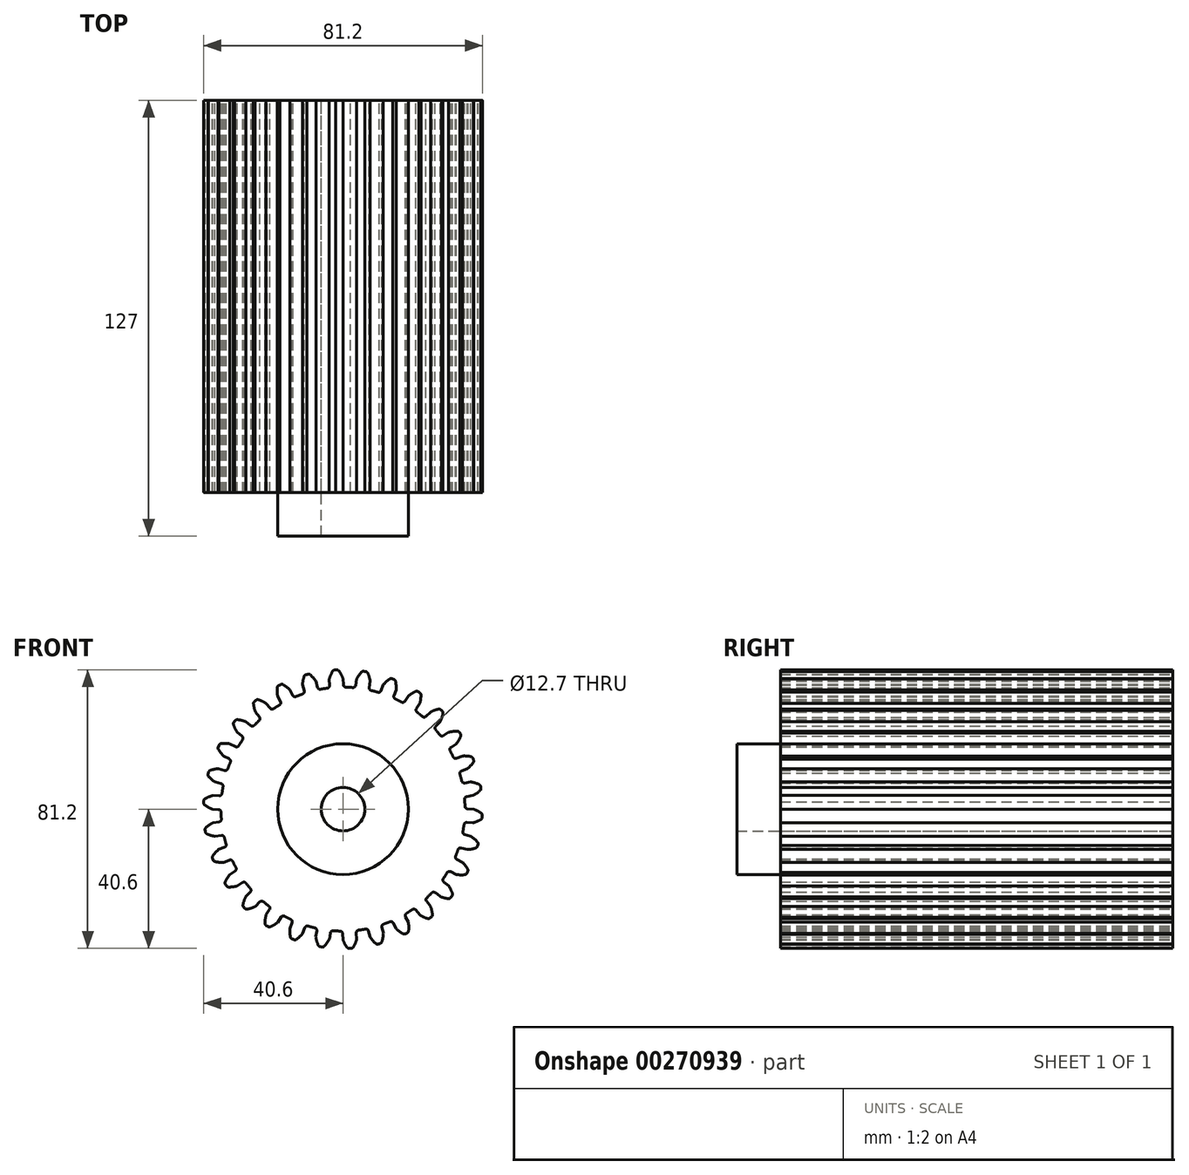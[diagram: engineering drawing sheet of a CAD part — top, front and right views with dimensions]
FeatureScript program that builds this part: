
annotation { "Feature Type Name" : "Feature", "Feature Type Description" : "" }
export const myFeature = defineFeature(function(context is Context, id is Id, definition is map)
    precondition{}
    {
        {
            var Q0;
            Q0=qCreatedBy(makeId("Front.planeOp"),FACE);
            var sketch = newSketch(context, id + "F0", { "sketchPlane" : qUnion([Q0])});
            skCircle(sketch, "E0", {"center": v(0, 0) * mm, "radius": 6.35 * mm});
            skArc(sketch, "E1", {"start": v(-11.8, 33.55) * mm, "mid": v(-12.74, 33.2) * mm, "end": v(-13.69, 32.82) * mm});
            skArc(sketch, "E2.trimOffspring", {"start": v(0, 38.1) * mm, "mid": v(-0.51, 39.23) * mm, "end": v(-1.18, 40.29) * mm});
            skLineSegment(sketch, "E3", {"start": v(-1.82, 40.6) * mm, "end": v(-2.13, 40.6) * mm});
            skLineSegment(sketch, "E4", {"start": v(0, 38.1) * mm, "end": v(0.1, 36.27) * mm});
            skLineSegment(sketch, "E5.MirrorCS", {"start": v(-2.43, 40.57) * mm, "end": v(-2.13, 40.6) * mm});
            skArc(sketch, "E6.MirrorCS", {"start": v(-4, 37.9) * mm, "mid": v(-3.59, 39.07) * mm, "end": v(-3.04, 40.2) * mm});
            skLineSegment(sketch, "E7.MirrorCS", {"start": v(-4, 37.9) * mm, "end": v(-3.9, 36.06) * mm});
            skArc(sketch, "E8.1.0", {"start": v(-11.78, 36.23) * mm, "mid": v(-11.63, 37.47) * mm, "end": v(-11.33, 38.68) * mm});
            skLineSegment(sketch, "E8.1.1", {"start": v(-11.78, 36.23) * mm, "end": v(-11.3, 34.46) * mm});
            skLineSegment(sketch, "E8.1.2", {"start": v(-7.91, 37.27) * mm, "end": v(-7.44, 35.5) * mm});
            skArc(sketch, "E8.1.3", {"start": v(-7.91, 37.27) * mm, "mid": v(-8.66, 38.27) * mm, "end": v(-9.53, 39.16) * mm});
            skLineSegment(sketch, "E8.1.4", {"start": v(-10.23, 39.33) * mm, "end": v(-10.52, 39.26) * mm});
            skLineSegment(sketch, "E8.1.5", {"start": v(-10.81, 39.18) * mm, "end": v(-10.52, 39.26) * mm});
            skArc(sketch, "E8.2.0", {"start": v(-19.06, 33) * mm, "mid": v(-19.17, 34.23) * mm, "end": v(-19.12, 35.48) * mm});
            skLineSegment(sketch, "E8.2.1", {"start": v(-19.06, 33) * mm, "end": v(-18.23, 31.36) * mm});
            skLineSegment(sketch, "E8.2.2", {"start": v(-15.49, 34.8) * mm, "end": v(-14.66, 33.18) * mm});
            skArc(sketch, "E8.2.3", {"start": v(-15.49, 34.8) * mm, "mid": v(-16.43, 35.63) * mm, "end": v(-17.47, 36.32) * mm});
            skLineSegment(sketch, "E8.2.4", {"start": v(-18.18, 36.35) * mm, "end": v(-18.45, 36.22) * mm});
            skLineSegment(sketch, "E8.2.5", {"start": v(-18.72, 36.07) * mm, "end": v(-18.45, 36.22) * mm});
            skArc(sketch, "E9.2.3.0", {"start": v(-25.5, 28.3) * mm, "mid": v(-25.87, 29.5) * mm, "end": v(-26.08, 30.73) * mm});
            skLineSegment(sketch, "E9.4.3.0", {"start": v(-25.5, 28.3) * mm, "end": v(-24.35, 26.89) * mm});
            skLineSegment(sketch, "E9.7.3.0", {"start": v(-22.39, 30.83) * mm, "end": v(-21.24, 29.4) * mm});
            skArc(sketch, "E9.10.3.0", {"start": v(-22.39, 30.83) * mm, "mid": v(-23.48, 31.44) * mm, "end": v(-24.64, 31.9) * mm});
            skLineSegment(sketch, "E9.14.3.0", {"start": v(-25.34, 31.77) * mm, "end": v(-25.58, 31.59) * mm});
            skLineSegment(sketch, "E9.17.3.0", {"start": v(-25.81, 31.4) * mm, "end": v(-25.58, 31.59) * mm});
            skArc(sketch, "E9.2.4.0", {"start": v(-30.83, 22.39) * mm, "mid": v(-31.44, 23.48) * mm, "end": v(-31.9, 24.64) * mm});
            skLineSegment(sketch, "E9.4.4.0", {"start": v(-30.83, 22.39) * mm, "end": v(-29.4, 21.24) * mm});
            skLineSegment(sketch, "E9.7.4.0", {"start": v(-28.3, 25.5) * mm, "end": v(-26.89, 24.35) * mm});
            skArc(sketch, "E9.10.4.0", {"start": v(-28.3, 25.5) * mm, "mid": v(-29.5, 25.87) * mm, "end": v(-30.73, 26.08) * mm});
            skLineSegment(sketch, "E9.14.4.0", {"start": v(-31.4, 25.81) * mm, "end": v(-31.59, 25.58) * mm});
            skLineSegment(sketch, "E9.17.4.0", {"start": v(-31.77, 25.34) * mm, "end": v(-31.59, 25.58) * mm});
            skArc(sketch, "E9.2.5.0", {"start": v(-34.8, 15.49) * mm, "mid": v(-35.63, 16.43) * mm, "end": v(-36.32, 17.47) * mm});
            skLineSegment(sketch, "E9.4.5.0", {"start": v(-34.8, 15.49) * mm, "end": v(-33.18, 14.66) * mm});
            skLineSegment(sketch, "E9.7.5.0", {"start": v(-33, 19.06) * mm, "end": v(-31.36, 18.23) * mm});
            skArc(sketch, "E9.10.5.0", {"start": v(-33, 19.06) * mm, "mid": v(-34.23, 19.17) * mm, "end": v(-35.48, 19.12) * mm});
            skLineSegment(sketch, "E9.14.5.0", {"start": v(-36.07, 18.72) * mm, "end": v(-36.22, 18.45) * mm});
            skLineSegment(sketch, "E9.17.5.0", {"start": v(-36.35, 18.18) * mm, "end": v(-36.22, 18.45) * mm});
            skArc(sketch, "E9.2.6.0", {"start": v(-37.27, 7.91) * mm, "mid": v(-38.27, 8.66) * mm, "end": v(-39.16, 9.53) * mm});
            skLineSegment(sketch, "E9.4.6.0", {"start": v(-37.27, 7.91) * mm, "end": v(-35.5, 7.44) * mm});
            skLineSegment(sketch, "E9.7.6.0", {"start": v(-36.23, 11.78) * mm, "end": v(-34.46, 11.3) * mm});
            skArc(sketch, "E9.10.6.0", {"start": v(-36.23, 11.78) * mm, "mid": v(-37.47, 11.63) * mm, "end": v(-38.68, 11.33) * mm});
            skLineSegment(sketch, "E9.14.6.0", {"start": v(-39.18, 10.81) * mm, "end": v(-39.26, 10.52) * mm});
            skLineSegment(sketch, "E9.17.6.0", {"start": v(-39.33, 10.23) * mm, "end": v(-39.26, 10.52) * mm});
            skArc(sketch, "E9.2.7.0", {"start": v(-38.1, 0) * mm, "mid": v(-39.23, 0.51) * mm, "end": v(-40.29, 1.18) * mm});
            skLineSegment(sketch, "E9.4.7.0", {"start": v(-38.1, 0) * mm, "end": v(-36.27, -0.1) * mm});
            skLineSegment(sketch, "E9.7.7.0", {"start": v(-37.9, 4) * mm, "end": v(-36.06, 3.9) * mm});
            skArc(sketch, "E9.10.7.0", {"start": v(-37.9, 4) * mm, "mid": v(-39.07, 3.59) * mm, "end": v(-40.2, 3.04) * mm});
            skLineSegment(sketch, "E9.14.7.0", {"start": v(-40.57, 2.43) * mm, "end": v(-40.6, 2.13) * mm});
            skLineSegment(sketch, "E9.17.7.0", {"start": v(-40.6, 1.82) * mm, "end": v(-40.6, 2.13) * mm});
            skArc(sketch, "E9.2.8.0", {"start": v(-37.27, -7.93) * mm, "mid": v(-38.48, -7.65) * mm, "end": v(-39.65, -7.22) * mm});
            skLineSegment(sketch, "E9.4.8.0", {"start": v(-37.27, -7.93) * mm, "end": v(-35.46, -7.64) * mm});
            skLineSegment(sketch, "E9.7.8.0", {"start": v(-37.9, -3.97) * mm, "end": v(-36.08, -3.69) * mm});
            skArc(sketch, "E9.10.8.0", {"start": v(-37.9, -3.97) * mm, "mid": v(-38.96, -4.61) * mm, "end": v(-39.94, -5.39) * mm});
            skLineSegment(sketch, "E9.14.8.0", {"start": v(-40.19, -6.06) * mm, "end": v(-40.15, -6.36) * mm});
            skLineSegment(sketch, "E9.17.8.0", {"start": v(-40.1, -6.66) * mm, "end": v(-40.15, -6.36) * mm});
            skArc(sketch, "E9.2.9.0", {"start": v(-34.8, -15.5) * mm, "mid": v(-36.05, -15.49) * mm, "end": v(-37.29, -15.3) * mm});
            skLineSegment(sketch, "E9.4.9.0", {"start": v(-34.8, -15.5) * mm, "end": v(-33.1, -14.85) * mm});
            skLineSegment(sketch, "E9.7.9.0", {"start": v(-36.24, -11.77) * mm, "end": v(-34.53, -11.1) * mm});
            skArc(sketch, "E9.10.9.0", {"start": v(-36.24, -11.77) * mm, "mid": v(-37.15, -12.61) * mm, "end": v(-37.95, -13.57) * mm});
            skLineSegment(sketch, "E9.14.9.0", {"start": v(-38.05, -14.28) * mm, "end": v(-37.95, -14.57) * mm});
            skLineSegment(sketch, "E9.17.9.0", {"start": v(-37.83, -14.85) * mm, "end": v(-37.95, -14.57) * mm});
            skArc(sketch, "E9.2.10.0", {"start": v(-30.82, -22.4) * mm, "mid": v(-32.04, -22.64) * mm, "end": v(-33.29, -22.73) * mm});
            skLineSegment(sketch, "E9.4.10.0", {"start": v(-30.82, -22.4) * mm, "end": v(-29.28, -21.4) * mm});
            skLineSegment(sketch, "E9.7.10.0", {"start": v(-33, -19.04) * mm, "end": v(-31.46, -18.05) * mm});
            skArc(sketch, "E9.10.10.0", {"start": v(-33, -19.04) * mm, "mid": v(-33.72, -20.06) * mm, "end": v(-34.3, -21.17) * mm});
            skLineSegment(sketch, "E9.14.10.0", {"start": v(-34.25, -21.88) * mm, "end": v(-34.09, -22.14) * mm});
            skLineSegment(sketch, "E9.17.10.0", {"start": v(-33.92, -22.39) * mm, "end": v(-34.09, -22.14) * mm});
            skArc(sketch, "E9.2.11.0", {"start": v(-25.49, -28.32) * mm, "mid": v(-26.63, -28.81) * mm, "end": v(-27.84, -29.15) * mm});
            skLineSegment(sketch, "E9.4.11.0", {"start": v(-25.49, -28.32) * mm, "end": v(-24.2, -27.03) * mm});
            skLineSegment(sketch, "E9.7.11.0", {"start": v(-28.32, -25.49) * mm, "end": v(-27.03, -24.2) * mm});
            skArc(sketch, "E9.10.11.0", {"start": v(-28.32, -25.49) * mm, "mid": v(-28.81, -26.63) * mm, "end": v(-29.15, -27.84) * mm});
            skLineSegment(sketch, "E9.14.11.0", {"start": v(-28.95, -28.52) * mm, "end": v(-28.74, -28.74) * mm});
            skLineSegment(sketch, "E9.17.11.0", {"start": v(-28.52, -28.95) * mm, "end": v(-28.74, -28.74) * mm});
            skArc(sketch, "E9.2.12.0", {"start": v(-19.04, -33) * mm, "mid": v(-20.06, -33.72) * mm, "end": v(-21.17, -34.3) * mm});
            skLineSegment(sketch, "E9.4.12.0", {"start": v(-19.04, -33) * mm, "end": v(-18.05, -31.46) * mm});
            skLineSegment(sketch, "E9.7.12.0", {"start": v(-22.4, -30.82) * mm, "end": v(-21.4, -29.28) * mm});
            skArc(sketch, "E9.10.12.0", {"start": v(-22.4, -30.82) * mm, "mid": v(-22.64, -32.04) * mm, "end": v(-22.73, -33.29) * mm});
            skLineSegment(sketch, "E9.14.12.0", {"start": v(-22.39, -33.92) * mm, "end": v(-22.14, -34.09) * mm});
            skLineSegment(sketch, "E9.17.12.0", {"start": v(-21.88, -34.25) * mm, "end": v(-22.14, -34.09) * mm});
            skArc(sketch, "E9.2.13.0", {"start": v(-11.77, -36.24) * mm, "mid": v(-12.61, -37.15) * mm, "end": v(-13.57, -37.95) * mm});
            skLineSegment(sketch, "E9.4.13.0", {"start": v(-11.77, -36.24) * mm, "end": v(-11.1, -34.53) * mm});
            skLineSegment(sketch, "E9.7.13.0", {"start": v(-15.5, -34.8) * mm, "end": v(-14.85, -33.1) * mm});
            skArc(sketch, "E9.10.13.0", {"start": v(-15.5, -34.8) * mm, "mid": v(-15.49, -36.05) * mm, "end": v(-15.3, -37.29) * mm});
            skLineSegment(sketch, "E9.14.13.0", {"start": v(-14.85, -37.83) * mm, "end": v(-14.57, -37.95) * mm});
            skLineSegment(sketch, "E9.17.13.0", {"start": v(-14.28, -38.05) * mm, "end": v(-14.57, -37.95) * mm});
            skArc(sketch, "E9.2.14.0", {"start": v(-3.97, -37.9) * mm, "mid": v(-4.61, -38.96) * mm, "end": v(-5.39, -39.94) * mm});
            skLineSegment(sketch, "E9.4.14.0", {"start": v(-3.97, -37.9) * mm, "end": v(-3.69, -36.08) * mm});
            skLineSegment(sketch, "E9.7.14.0", {"start": v(-7.93, -37.27) * mm, "end": v(-7.64, -35.46) * mm});
            skArc(sketch, "E9.10.14.0", {"start": v(-7.93, -37.27) * mm, "mid": v(-7.65, -38.48) * mm, "end": v(-7.22, -39.65) * mm});
            skLineSegment(sketch, "E9.14.14.0", {"start": v(-6.66, -40.1) * mm, "end": v(-6.36, -40.15) * mm});
            skLineSegment(sketch, "E9.17.14.0", {"start": v(-6.06, -40.19) * mm, "end": v(-6.36, -40.15) * mm});
            skArc(sketch, "E9.2.15.0", {"start": v(4, -37.9) * mm, "mid": v(3.59, -39.07) * mm, "end": v(3.04, -40.2) * mm});
            skLineSegment(sketch, "E9.4.15.0", {"start": v(4, -37.9) * mm, "end": v(3.9, -36.06) * mm});
            skLineSegment(sketch, "E9.7.15.0", {"start": v(0, -38.1) * mm, "end": v(-0.1, -36.27) * mm});
            skArc(sketch, "E9.10.15.0", {"start": v(0, -38.1) * mm, "mid": v(0.51, -39.23) * mm, "end": v(1.18, -40.29) * mm});
            skLineSegment(sketch, "E9.14.15.0", {"start": v(1.82, -40.6) * mm, "end": v(2.13, -40.6) * mm});
            skLineSegment(sketch, "E9.17.15.0", {"start": v(2.43, -40.57) * mm, "end": v(2.13, -40.6) * mm});
            skArc(sketch, "E9.2.16.0", {"start": v(11.78, -36.23) * mm, "mid": v(11.63, -37.47) * mm, "end": v(11.33, -38.68) * mm});
            skLineSegment(sketch, "E9.4.16.0", {"start": v(11.78, -36.23) * mm, "end": v(11.3, -34.46) * mm});
            skLineSegment(sketch, "E9.7.16.0", {"start": v(7.91, -37.27) * mm, "end": v(7.44, -35.5) * mm});
            skArc(sketch, "E9.10.16.0", {"start": v(7.91, -37.27) * mm, "mid": v(8.66, -38.27) * mm, "end": v(9.53, -39.16) * mm});
            skLineSegment(sketch, "E9.14.16.0", {"start": v(10.23, -39.33) * mm, "end": v(10.52, -39.26) * mm});
            skLineSegment(sketch, "E9.17.16.0", {"start": v(10.81, -39.18) * mm, "end": v(10.52, -39.26) * mm});
            skArc(sketch, "E9.2.17.0", {"start": v(19.06, -33) * mm, "mid": v(19.17, -34.23) * mm, "end": v(19.12, -35.48) * mm});
            skLineSegment(sketch, "E9.4.17.0", {"start": v(19.06, -33) * mm, "end": v(18.23, -31.36) * mm});
            skLineSegment(sketch, "E9.7.17.0", {"start": v(15.49, -34.8) * mm, "end": v(14.66, -33.18) * mm});
            skArc(sketch, "E9.10.17.0", {"start": v(15.49, -34.8) * mm, "mid": v(16.43, -35.63) * mm, "end": v(17.47, -36.32) * mm});
            skLineSegment(sketch, "E9.14.17.0", {"start": v(18.18, -36.35) * mm, "end": v(18.45, -36.22) * mm});
            skLineSegment(sketch, "E9.17.17.0", {"start": v(18.72, -36.07) * mm, "end": v(18.45, -36.22) * mm});
            skArc(sketch, "E9.2.18.0", {"start": v(25.5, -28.3) * mm, "mid": v(25.87, -29.5) * mm, "end": v(26.08, -30.73) * mm});
            skLineSegment(sketch, "E9.4.18.0", {"start": v(25.5, -28.3) * mm, "end": v(24.35, -26.89) * mm});
            skLineSegment(sketch, "E9.7.18.0", {"start": v(22.39, -30.83) * mm, "end": v(21.24, -29.4) * mm});
            skArc(sketch, "E9.10.18.0", {"start": v(22.39, -30.83) * mm, "mid": v(23.48, -31.44) * mm, "end": v(24.64, -31.9) * mm});
            skLineSegment(sketch, "E9.14.18.0", {"start": v(25.34, -31.77) * mm, "end": v(25.58, -31.59) * mm});
            skLineSegment(sketch, "E9.17.18.0", {"start": v(25.81, -31.4) * mm, "end": v(25.58, -31.59) * mm});
            skArc(sketch, "E9.2.19.0", {"start": v(30.83, -22.39) * mm, "mid": v(31.44, -23.48) * mm, "end": v(31.9, -24.64) * mm});
            skLineSegment(sketch, "E9.4.19.0", {"start": v(30.83, -22.39) * mm, "end": v(29.4, -21.24) * mm});
            skLineSegment(sketch, "E9.7.19.0", {"start": v(28.3, -25.5) * mm, "end": v(26.89, -24.35) * mm});
            skArc(sketch, "E9.10.19.0", {"start": v(28.3, -25.5) * mm, "mid": v(29.5, -25.87) * mm, "end": v(30.73, -26.08) * mm});
            skLineSegment(sketch, "E9.14.19.0", {"start": v(31.4, -25.81) * mm, "end": v(31.59, -25.58) * mm});
            skLineSegment(sketch, "E9.17.19.0", {"start": v(31.77, -25.34) * mm, "end": v(31.59, -25.58) * mm});
            skArc(sketch, "E9.2.20.0", {"start": v(34.8, -15.49) * mm, "mid": v(35.63, -16.43) * mm, "end": v(36.32, -17.47) * mm});
            skLineSegment(sketch, "E9.4.20.0", {"start": v(34.8, -15.49) * mm, "end": v(33.18, -14.66) * mm});
            skLineSegment(sketch, "E9.7.20.0", {"start": v(33, -19.06) * mm, "end": v(31.36, -18.23) * mm});
            skArc(sketch, "E9.10.20.0", {"start": v(33, -19.06) * mm, "mid": v(34.23, -19.17) * mm, "end": v(35.48, -19.12) * mm});
            skLineSegment(sketch, "E9.14.20.0", {"start": v(36.07, -18.72) * mm, "end": v(36.22, -18.45) * mm});
            skLineSegment(sketch, "E9.17.20.0", {"start": v(36.35, -18.18) * mm, "end": v(36.22, -18.45) * mm});
            skArc(sketch, "E9.2.21.0", {"start": v(37.27, -7.91) * mm, "mid": v(38.27, -8.66) * mm, "end": v(39.16, -9.53) * mm});
            skLineSegment(sketch, "E9.4.21.0", {"start": v(37.27, -7.91) * mm, "end": v(35.5, -7.44) * mm});
            skLineSegment(sketch, "E9.7.21.0", {"start": v(36.23, -11.78) * mm, "end": v(34.46, -11.3) * mm});
            skArc(sketch, "E9.10.21.0", {"start": v(36.23, -11.78) * mm, "mid": v(37.47, -11.63) * mm, "end": v(38.68, -11.33) * mm});
            skLineSegment(sketch, "E9.14.21.0", {"start": v(39.18, -10.81) * mm, "end": v(39.26, -10.52) * mm});
            skLineSegment(sketch, "E9.17.21.0", {"start": v(39.33, -10.23) * mm, "end": v(39.26, -10.52) * mm});
            skArc(sketch, "E9.2.22.0", {"start": v(38.1, 0) * mm, "mid": v(39.23, -0.51) * mm, "end": v(40.29, -1.18) * mm});
            skLineSegment(sketch, "E9.4.22.0", {"start": v(38.1, 0) * mm, "end": v(36.27, 0.1) * mm});
            skLineSegment(sketch, "E9.7.22.0", {"start": v(37.9, -4) * mm, "end": v(36.06, -3.9) * mm});
            skArc(sketch, "E9.10.22.0", {"start": v(37.9, -4) * mm, "mid": v(39.07, -3.59) * mm, "end": v(40.2, -3.04) * mm});
            skLineSegment(sketch, "E9.14.22.0", {"start": v(40.57, -2.43) * mm, "end": v(40.59, -2.14) * mm});
            skLineSegment(sketch, "E9.17.22.0", {"start": v(40.6, -1.82) * mm, "end": v(40.6, -2.11) * mm});
            skArc(sketch, "E9.2.23.0", {"start": v(37.27, 7.93) * mm, "mid": v(38.48, 7.65) * mm, "end": v(39.65, 7.22) * mm});
            skLineSegment(sketch, "E9.4.23.0", {"start": v(37.27, 7.93) * mm, "end": v(35.46, 7.64) * mm});
            skLineSegment(sketch, "E9.7.23.0", {"start": v(37.9, 3.97) * mm, "end": v(36.08, 3.69) * mm});
            skArc(sketch, "E9.10.23.0", {"start": v(37.9, 3.97) * mm, "mid": v(38.96, 4.61) * mm, "end": v(39.94, 5.39) * mm});
            skLineSegment(sketch, "E9.14.23.0", {"start": v(40.19, 6.06) * mm, "end": v(40.15, 6.36) * mm});
            skLineSegment(sketch, "E9.17.23.0", {"start": v(40.1, 6.66) * mm, "end": v(40.15, 6.36) * mm});
            skArc(sketch, "E9.2.24.0", {"start": v(34.8, 15.5) * mm, "mid": v(36.05, 15.49) * mm, "end": v(37.29, 15.3) * mm});
            skLineSegment(sketch, "E9.4.24.0", {"start": v(34.8, 15.5) * mm, "end": v(33.1, 14.85) * mm});
            skLineSegment(sketch, "E9.7.24.0", {"start": v(36.24, 11.77) * mm, "end": v(34.53, 11.1) * mm});
            skArc(sketch, "E9.10.24.0", {"start": v(36.24, 11.77) * mm, "mid": v(37.15, 12.61) * mm, "end": v(37.95, 13.57) * mm});
            skLineSegment(sketch, "E9.14.24.0", {"start": v(38.05, 14.28) * mm, "end": v(37.95, 14.57) * mm});
            skLineSegment(sketch, "E9.17.24.0", {"start": v(37.83, 14.85) * mm, "end": v(37.95, 14.57) * mm});
            skArc(sketch, "E9.2.25.0", {"start": v(30.82, 22.4) * mm, "mid": v(32.04, 22.64) * mm, "end": v(33.29, 22.73) * mm});
            skLineSegment(sketch, "E9.4.25.0", {"start": v(30.82, 22.4) * mm, "end": v(29.28, 21.4) * mm});
            skLineSegment(sketch, "E9.7.25.0", {"start": v(33, 19.04) * mm, "end": v(31.46, 18.05) * mm});
            skArc(sketch, "E9.10.25.0", {"start": v(33, 19.04) * mm, "mid": v(33.72, 20.06) * mm, "end": v(34.3, 21.17) * mm});
            skLineSegment(sketch, "E9.14.25.0", {"start": v(34.25, 21.88) * mm, "end": v(34.09, 22.14) * mm});
            skLineSegment(sketch, "E9.17.25.0", {"start": v(33.92, 22.39) * mm, "end": v(34.09, 22.14) * mm});
            skArc(sketch, "E9.2.26.0", {"start": v(25.49, 28.32) * mm, "mid": v(26.63, 28.81) * mm, "end": v(27.84, 29.15) * mm});
            skLineSegment(sketch, "E9.4.26.0", {"start": v(25.49, 28.32) * mm, "end": v(24.2, 27.03) * mm});
            skLineSegment(sketch, "E9.7.26.0", {"start": v(28.32, 25.49) * mm, "end": v(27.03, 24.2) * mm});
            skArc(sketch, "E9.10.26.0", {"start": v(28.32, 25.49) * mm, "mid": v(28.81, 26.63) * mm, "end": v(29.15, 27.84) * mm});
            skLineSegment(sketch, "E9.14.26.0", {"start": v(28.95, 28.52) * mm, "end": v(28.74, 28.74) * mm});
            skLineSegment(sketch, "E9.17.26.0", {"start": v(28.52, 28.95) * mm, "end": v(28.74, 28.74) * mm});
            skArc(sketch, "E9.2.27.0", {"start": v(19.04, 33) * mm, "mid": v(20.06, 33.72) * mm, "end": v(21.17, 34.3) * mm});
            skLineSegment(sketch, "E9.4.27.0", {"start": v(19.04, 33) * mm, "end": v(18.05, 31.46) * mm});
            skLineSegment(sketch, "E9.7.27.0", {"start": v(22.4, 30.82) * mm, "end": v(21.4, 29.28) * mm});
            skArc(sketch, "E9.10.27.0", {"start": v(22.4, 30.82) * mm, "mid": v(22.64, 32.04) * mm, "end": v(22.73, 33.29) * mm});
            skLineSegment(sketch, "E9.14.27.0", {"start": v(22.39, 33.92) * mm, "end": v(22.14, 34.09) * mm});
            skLineSegment(sketch, "E9.17.27.0", {"start": v(21.88, 34.25) * mm, "end": v(22.14, 34.09) * mm});
            skArc(sketch, "E9.2.28.0", {"start": v(11.77, 36.24) * mm, "mid": v(12.61, 37.15) * mm, "end": v(13.57, 37.95) * mm});
            skLineSegment(sketch, "E9.4.28.0", {"start": v(11.77, 36.24) * mm, "end": v(11.1, 34.53) * mm});
            skLineSegment(sketch, "E9.7.28.0", {"start": v(15.5, 34.8) * mm, "end": v(14.85, 33.1) * mm});
            skArc(sketch, "E9.10.28.0", {"start": v(15.5, 34.8) * mm, "mid": v(15.49, 36.05) * mm, "end": v(15.3, 37.29) * mm});
            skLineSegment(sketch, "E9.14.28.0", {"start": v(14.85, 37.83) * mm, "end": v(14.57, 37.95) * mm});
            skLineSegment(sketch, "E9.17.28.0", {"start": v(14.28, 38.05) * mm, "end": v(14.57, 37.95) * mm});
            skArc(sketch, "E9.2.29.0", {"start": v(3.97, 37.9) * mm, "mid": v(4.61, 38.96) * mm, "end": v(5.39, 39.94) * mm});
            skLineSegment(sketch, "E9.4.29.0", {"start": v(3.97, 37.9) * mm, "end": v(3.69, 36.08) * mm});
            skLineSegment(sketch, "E9.7.29.0", {"start": v(7.93, 37.27) * mm, "end": v(7.64, 35.46) * mm});
            skArc(sketch, "E9.10.29.0", {"start": v(7.93, 37.27) * mm, "mid": v(7.65, 38.48) * mm, "end": v(7.22, 39.65) * mm});
            skLineSegment(sketch, "E9.14.29.0", {"start": v(6.66, 40.1) * mm, "end": v(6.36, 40.15) * mm});
            skLineSegment(sketch, "E9.17.29.0", {"start": v(6.06, 40.19) * mm, "end": v(6.36, 40.15) * mm});
            skArc(sketch, "E10.trimOffspring", {"start": v(-4.56, 35.27) * mm, "mid": v(-5.56, 35.12) * mm, "end": v(-6.56, 34.95) * mm});
            skArc(sketch, "E11.trimOffspring", {"start": v(2.87, 35.44) * mm, "mid": v(1.86, 35.51) * mm, "end": v(0.85, 35.55) * mm});
            skArc(sketch, "E12.trimOffspring", {"start": v(10.18, 34.07) * mm, "mid": v(9.2, 34.35) * mm, "end": v(8.22, 34.6) * mm});
            skArc(sketch, "E13.trimOffspring", {"start": v(17.04, 31.21) * mm, "mid": v(16.14, 31.68) * mm, "end": v(15.23, 32.13) * mm});
            skArc(sketch, "E14.trimOffspring", {"start": v(23.16, 26.99) * mm, "mid": v(22.38, 27.64) * mm, "end": v(21.58, 28.26) * mm});
            skArc(sketch, "E15.trimOffspring", {"start": v(28.26, 21.58) * mm, "mid": v(27.64, 22.38) * mm, "end": v(26.99, 23.16) * mm});
            skArc(sketch, "E16.trimOffspring", {"start": v(32.13, 15.23) * mm, "mid": v(31.68, 16.14) * mm, "end": v(31.21, 17.04) * mm});
            skArc(sketch, "E17.trimOffspring", {"start": v(34.6, 8.22) * mm, "mid": v(34.35, 9.2) * mm, "end": v(34.07, 10.18) * mm});
            skArc(sketch, "E18.trimOffspring", {"start": v(35.55, 0.85) * mm, "mid": v(35.51, 1.86) * mm, "end": v(35.44, 2.87) * mm});
            skArc(sketch, "E19.trimOffspring", {"start": v(34.95, -6.56) * mm, "mid": v(35.12, -5.56) * mm, "end": v(35.27, -4.56) * mm});
            skArc(sketch, "E20.trimOffspring", {"start": v(32.82, -13.69) * mm, "mid": v(33.2, -12.74) * mm, "end": v(33.55, -11.8) * mm});
            skArc(sketch, "E21.trimOffspring", {"start": v(29.26, -20.21) * mm, "mid": v(29.82, -19.37) * mm, "end": v(30.36, -18.5) * mm});
            skArc(sketch, "E22.trimOffspring", {"start": v(24.42, -25.85) * mm, "mid": v(25.14, -25.14) * mm, "end": v(25.85, -24.42) * mm});
            skArc(sketch, "E23.trimOffspring", {"start": v(18.5, -30.36) * mm, "mid": v(19.37, -29.82) * mm, "end": v(20.21, -29.26) * mm});
            skArc(sketch, "E24.trimOffspring", {"start": v(11.8, -33.55) * mm, "mid": v(12.74, -33.2) * mm, "end": v(13.69, -32.82) * mm});
            skArc(sketch, "E25.trimOffspring", {"start": v(4.56, -35.27) * mm, "mid": v(5.56, -35.12) * mm, "end": v(6.56, -34.95) * mm});
            skArc(sketch, "E26.trimOffspring", {"start": v(-2.87, -35.44) * mm, "mid": v(-1.86, -35.51) * mm, "end": v(-0.85, -35.55) * mm});
            skArc(sketch, "E27.trimOffspring", {"start": v(-10.18, -34.07) * mm, "mid": v(-9.2, -34.35) * mm, "end": v(-8.22, -34.6) * mm});
            skArc(sketch, "E28.trimOffspring", {"start": v(-17.04, -31.21) * mm, "mid": v(-16.14, -31.68) * mm, "end": v(-15.23, -32.13) * mm});
            skArc(sketch, "E29.trimOffspring", {"start": v(-23.16, -26.99) * mm, "mid": v(-22.38, -27.64) * mm, "end": v(-21.58, -28.26) * mm});
            skArc(sketch, "E30.trimOffspring", {"start": v(-28.26, -21.58) * mm, "mid": v(-27.64, -22.38) * mm, "end": v(-26.99, -23.16) * mm});
            skArc(sketch, "E31.trimOffspring", {"start": v(-32.13, -15.23) * mm, "mid": v(-31.68, -16.14) * mm, "end": v(-31.21, -17.04) * mm});
            skArc(sketch, "E32.trimOffspring", {"start": v(-34.6, -8.22) * mm, "mid": v(-34.35, -9.2) * mm, "end": v(-34.07, -10.18) * mm});
            skArc(sketch, "E33.trimOffspring", {"start": v(-35.55, -0.85) * mm, "mid": v(-35.51, -1.86) * mm, "end": v(-35.44, -2.87) * mm});
            skArc(sketch, "E34.trimOffspring", {"start": v(-34.95, 6.56) * mm, "mid": v(-35.12, 5.56) * mm, "end": v(-35.27, 4.56) * mm});
            skArc(sketch, "E35.trimOffspring", {"start": v(-32.82, 13.69) * mm, "mid": v(-33.2, 12.74) * mm, "end": v(-33.55, 11.8) * mm});
            skArc(sketch, "E36.trimOffspring", {"start": v(-29.26, 20.21) * mm, "mid": v(-29.82, 19.37) * mm, "end": v(-30.36, 18.5) * mm});
            skArc(sketch, "E37.trimOffspring", {"start": v(-24.42, 25.85) * mm, "mid": v(-25.14, 25.14) * mm, "end": v(-25.85, 24.42) * mm});
            skArc(sketch, "E38.trimOffspring", {"start": v(-18.5, 30.36) * mm, "mid": v(-19.37, 29.82) * mm, "end": v(-20.21, 29.26) * mm});
            skPoint(sketch, "E39.visualSharp", {"position": v(-26.11, 31.14) * mm});
            skArc(sketch, "E39.filletArc", {"start": v(-25.81, 31.4) * mm, "mid": v(-26.03, 31.1) * mm, "end": v(-26.08, 30.73) * mm});
            skPoint(sketch, "E40.visualSharp", {"position": v(-25.03, 32.02) * mm});
            skArc(sketch, "E40.filletArc", {"start": v(-24.64, 31.9) * mm, "mid": v(-25, 31.92) * mm, "end": v(-25.34, 31.77) * mm});
            skPoint(sketch, "E41.visualSharp", {"position": v(-23.9, 26.33) * mm});
            skArc(sketch, "E41.filletArc", {"start": v(-24.42, 25.85) * mm, "mid": v(-24.18, 26.36) * mm, "end": v(-24.35, 26.89) * mm});
            skPoint(sketch, "E42.visualSharp", {"position": v(-20.79, 28.85) * mm});
            skArc(sketch, "E42.filletArc", {"start": v(-21.24, 29.4) * mm, "mid": v(-20.75, 29.13) * mm, "end": v(-20.21, 29.26) * mm});
            skPoint(sketch, "E43.visualSharp", {"position": v(-19.07, 35.89) * mm});
            skArc(sketch, "E43.filletArc", {"start": v(-18.72, 36.07) * mm, "mid": v(-19, 35.83) * mm, "end": v(-19.12, 35.48) * mm});
            skPoint(sketch, "E44.visualSharp", {"position": v(-17.83, 36.52) * mm});
            skArc(sketch, "E44.filletArc", {"start": v(-17.47, 36.32) * mm, "mid": v(-17.82, 36.43) * mm, "end": v(-18.18, 36.35) * mm});
            skPoint(sketch, "E45.visualSharp", {"position": v(-17.9, 30.72) * mm});
            skArc(sketch, "E45.filletArc", {"start": v(-18.5, 30.36) * mm, "mid": v(-18.17, 30.8) * mm, "end": v(-18.23, 31.36) * mm});
            skPoint(sketch, "E46.visualSharp", {"position": v(-14.33, 32.54) * mm});
            skArc(sketch, "E46.filletArc", {"start": v(-14.66, 33.18) * mm, "mid": v(-14.24, 32.8) * mm, "end": v(-13.69, 32.82) * mm});
            skPoint(sketch, "E47.visualSharp", {"position": v(-11.2, 39.07) * mm});
            skArc(sketch, "E47.filletArc", {"start": v(-10.81, 39.18) * mm, "mid": v(-11.13, 39) * mm, "end": v(-11.33, 38.68) * mm});
            skPoint(sketch, "E48.visualSharp", {"position": v(-9.84, 39.43) * mm});
            skArc(sketch, "E48.filletArc", {"start": v(-9.53, 39.16) * mm, "mid": v(-9.86, 39.33) * mm, "end": v(-10.23, 39.33) * mm});
            skPoint(sketch, "E49.visualSharp", {"position": v(-11.12, 33.78) * mm});
            skArc(sketch, "E49.filletArc", {"start": v(-11.8, 33.55) * mm, "mid": v(-11.37, 33.91) * mm, "end": v(-11.3, 34.46) * mm});
            skPoint(sketch, "E50.visualSharp", {"position": v(-7.25, 34.81) * mm});
            skArc(sketch, "E50.filletArc", {"start": v(-7.44, 35.5) * mm, "mid": v(-7.1, 35.05) * mm, "end": v(-6.56, 34.95) * mm});
            skPoint(sketch, "E51.visualSharp", {"position": v(-3.86, 35.35) * mm});
            skArc(sketch, "E51.filletArc", {"start": v(-4.56, 35.27) * mm, "mid": v(-4.07, 35.53) * mm, "end": v(-3.9, 36.06) * mm});
            skPoint(sketch, "E52.visualSharp", {"position": v(-2.82, 40.54) * mm});
            skArc(sketch, "E52.filletArc", {"start": v(-2.43, 40.57) * mm, "mid": v(-2.78, 40.46) * mm, "end": v(-3.04, 40.2) * mm});
            skPoint(sketch, "E53.visualSharp", {"position": v(-1.43, 40.61) * mm});
            skArc(sketch, "E53.filletArc", {"start": v(-1.18, 40.29) * mm, "mid": v(-1.46, 40.52) * mm, "end": v(-1.82, 40.6) * mm});
            skPoint(sketch, "E54.visualSharp", {"position": v(0.14, 35.56) * mm});
            skArc(sketch, "E54.filletArc", {"start": v(0.1, 36.27) * mm, "mid": v(0.33, 35.77) * mm, "end": v(0.85, 35.55) * mm});
            skPoint(sketch, "E55.visualSharp", {"position": v(3.58, 35.38) * mm});
            skArc(sketch, "E55.filletArc", {"start": v(2.87, 35.44) * mm, "mid": v(3.4, 35.6) * mm, "end": v(3.69, 36.08) * mm});
            skPoint(sketch, "E56.visualSharp", {"position": v(7.53, 34.75) * mm});
            skArc(sketch, "E56.filletArc", {"start": v(7.64, 35.46) * mm, "mid": v(7.76, 34.91) * mm, "end": v(8.22, 34.6) * mm});
            skPoint(sketch, "E57.visualSharp", {"position": v(7.05, 40.02) * mm});
            skArc(sketch, "E57.filletArc", {"start": v(7.22, 39.65) * mm, "mid": v(7, 39.94) * mm, "end": v(6.66, 40.1) * mm});
            skPoint(sketch, "E58.visualSharp", {"position": v(5.67, 40.24) * mm});
            skArc(sketch, "E58.filletArc", {"start": v(6.06, 40.19) * mm, "mid": v(5.7, 40.15) * mm, "end": v(5.39, 39.94) * mm});
            skPoint(sketch, "E59.visualSharp", {"position": v(10.85, 33.86) * mm});
            skArc(sketch, "E59.filletArc", {"start": v(10.18, 34.07) * mm, "mid": v(10.73, 34.12) * mm, "end": v(11.1, 34.53) * mm});
            skPoint(sketch, "E60.visualSharp", {"position": v(13.91, 38.19) * mm});
            skArc(sketch, "E60.filletArc", {"start": v(14.28, 38.05) * mm, "mid": v(13.91, 38.09) * mm, "end": v(13.57, 37.95) * mm});
            skPoint(sketch, "E61.visualSharp", {"position": v(15.21, 37.69) * mm});
            skArc(sketch, "E61.filletArc", {"start": v(15.3, 37.29) * mm, "mid": v(15.15, 37.62) * mm, "end": v(14.85, 37.83) * mm});
            skPoint(sketch, "E62.visualSharp", {"position": v(14.6, 32.43) * mm});
            skArc(sketch, "E62.filletArc", {"start": v(14.85, 33.1) * mm, "mid": v(14.85, 32.54) * mm, "end": v(15.23, 32.13) * mm});
            skPoint(sketch, "E63.visualSharp", {"position": v(17.66, 30.87) * mm});
            skArc(sketch, "E63.filletArc", {"start": v(17.04, 31.21) * mm, "mid": v(17.6, 31.14) * mm, "end": v(18.05, 31.46) * mm});
            skPoint(sketch, "E64.visualSharp", {"position": v(21.55, 34.46) * mm});
            skArc(sketch, "E64.filletArc", {"start": v(21.88, 34.25) * mm, "mid": v(21.53, 34.36) * mm, "end": v(21.17, 34.3) * mm});
            skPoint(sketch, "E65.visualSharp", {"position": v(22.72, 33.7) * mm});
            skArc(sketch, "E65.filletArc", {"start": v(22.73, 33.29) * mm, "mid": v(22.64, 33.65) * mm, "end": v(22.39, 33.92) * mm});
            skPoint(sketch, "E66.visualSharp", {"position": v(21.02, 28.69) * mm});
            skArc(sketch, "E66.filletArc", {"start": v(21.4, 29.28) * mm, "mid": v(21.3, 28.74) * mm, "end": v(21.58, 28.26) * mm});
            skPoint(sketch, "E67.visualSharp", {"position": v(23.69, 26.52) * mm});
            skArc(sketch, "E67.filletArc", {"start": v(23.16, 26.99) * mm, "mid": v(23.68, 26.8) * mm, "end": v(24.2, 27.03) * mm});
            skPoint(sketch, "E68.visualSharp", {"position": v(28.24, 29.23) * mm});
            skArc(sketch, "E68.filletArc", {"start": v(28.52, 28.95) * mm, "mid": v(28.2, 29.14) * mm, "end": v(27.84, 29.15) * mm});
            skPoint(sketch, "E69.visualSharp", {"position": v(29.23, 28.24) * mm});
            skArc(sketch, "E69.filletArc", {"start": v(29.15, 27.84) * mm, "mid": v(29.14, 28.2) * mm, "end": v(28.95, 28.52) * mm});
            skPoint(sketch, "E70.visualSharp", {"position": v(26.52, 23.69) * mm});
            skArc(sketch, "E70.filletArc", {"start": v(27.03, 24.2) * mm, "mid": v(26.8, 23.68) * mm, "end": v(26.99, 23.16) * mm});
            skPoint(sketch, "E71.visualSharp", {"position": v(28.69, 21.02) * mm});
            skArc(sketch, "E71.filletArc", {"start": v(28.26, 21.58) * mm, "mid": v(28.74, 21.3) * mm, "end": v(29.28, 21.4) * mm});
            skPoint(sketch, "E72.visualSharp", {"position": v(33.7, 22.72) * mm});
            skArc(sketch, "E72.filletArc", {"start": v(33.92, 22.39) * mm, "mid": v(33.65, 22.64) * mm, "end": v(33.29, 22.73) * mm});
            skPoint(sketch, "E73.visualSharp", {"position": v(34.46, 21.55) * mm});
            skArc(sketch, "E73.filletArc", {"start": v(34.3, 21.17) * mm, "mid": v(34.36, 21.53) * mm, "end": v(34.25, 21.88) * mm});
            skPoint(sketch, "E74.visualSharp", {"position": v(30.87, 17.66) * mm});
            skArc(sketch, "E74.filletArc", {"start": v(31.46, 18.05) * mm, "mid": v(31.14, 17.6) * mm, "end": v(31.21, 17.04) * mm});
            skPoint(sketch, "E75.visualSharp", {"position": v(32.43, 14.6) * mm});
            skArc(sketch, "E75.filletArc", {"start": v(32.13, 15.23) * mm, "mid": v(32.54, 14.85) * mm, "end": v(33.1, 14.85) * mm});
            skPoint(sketch, "E76.visualSharp", {"position": v(37.69, 15.21) * mm});
            skArc(sketch, "E76.filletArc", {"start": v(37.83, 14.85) * mm, "mid": v(37.62, 15.15) * mm, "end": v(37.29, 15.3) * mm});
            skPoint(sketch, "E77.visualSharp", {"position": v(38.19, 13.91) * mm});
            skArc(sketch, "E77.filletArc", {"start": v(37.95, 13.57) * mm, "mid": v(38.09, 13.91) * mm, "end": v(38.05, 14.28) * mm});
            skPoint(sketch, "E78.visualSharp", {"position": v(33.86, 10.85) * mm});
            skArc(sketch, "E78.filletArc", {"start": v(34.53, 11.1) * mm, "mid": v(34.12, 10.73) * mm, "end": v(34.07, 10.18) * mm});
            skPoint(sketch, "E79.visualSharp", {"position": v(34.75, 7.53) * mm});
            skArc(sketch, "E79.filletArc", {"start": v(34.6, 8.22) * mm, "mid": v(34.91, 7.76) * mm, "end": v(35.46, 7.64) * mm});
            skPoint(sketch, "E80.visualSharp", {"position": v(40.02, 7.05) * mm});
            skArc(sketch, "E80.filletArc", {"start": v(40.1, 6.66) * mm, "mid": v(39.94, 7) * mm, "end": v(39.65, 7.22) * mm});
            skPoint(sketch, "E81.visualSharp", {"position": v(40.24, 5.67) * mm});
            skArc(sketch, "E81.filletArc", {"start": v(39.94, 5.39) * mm, "mid": v(40.15, 5.7) * mm, "end": v(40.19, 6.06) * mm});
            skPoint(sketch, "E82.visualSharp", {"position": v(35.38, 3.58) * mm});
            skArc(sketch, "E82.filletArc", {"start": v(36.08, 3.69) * mm, "mid": v(35.6, 3.4) * mm, "end": v(35.44, 2.87) * mm});
            skPoint(sketch, "E83.visualSharp", {"position": v(35.56, 0.14) * mm});
            skArc(sketch, "E83.filletArc", {"start": v(35.55, 0.85) * mm, "mid": v(35.77, 0.33) * mm, "end": v(36.27, 0.1) * mm});
            skPoint(sketch, "E84.visualSharp", {"position": v(40.6, -2.13) * mm});
            skArc(sketch, "E84.filletArc", {"start": v(40.59, -2.14) * mm, "mid": v(40.6, -2.13) * mm, "end": v(40.6, -2.11) * mm});
            skPoint(sketch, "E85.visualSharp", {"position": v(35.35, -3.86) * mm});
            skArc(sketch, "E85.filletArc", {"start": v(36.06, -3.9) * mm, "mid": v(35.53, -4.07) * mm, "end": v(35.27, -4.56) * mm});
            skPoint(sketch, "E86.visualSharp", {"position": v(40.54, -2.82) * mm});
            skArc(sketch, "E86.filletArc", {"start": v(40.2, -3.04) * mm, "mid": v(40.46, -2.78) * mm, "end": v(40.57, -2.43) * mm});
            skPoint(sketch, "E87.visualSharp", {"position": v(40.61, -1.43) * mm});
            skArc(sketch, "E87.filletArc", {"start": v(40.6, -1.82) * mm, "mid": v(40.52, -1.46) * mm, "end": v(40.29, -1.18) * mm});
            skPoint(sketch, "E88.visualSharp", {"position": v(34.81, -7.25) * mm});
            skArc(sketch, "E88.filletArc", {"start": v(34.95, -6.56) * mm, "mid": v(35.05, -7.1) * mm, "end": v(35.5, -7.44) * mm});
            skPoint(sketch, "E89.visualSharp", {"position": v(39.43, -9.84) * mm});
            skArc(sketch, "E89.filletArc", {"start": v(39.33, -10.23) * mm, "mid": v(39.33, -9.86) * mm, "end": v(39.16, -9.53) * mm});
            skPoint(sketch, "E90.visualSharp", {"position": v(39.07, -11.2) * mm});
            skArc(sketch, "E90.filletArc", {"start": v(38.68, -11.33) * mm, "mid": v(39, -11.13) * mm, "end": v(39.18, -10.81) * mm});
            skPoint(sketch, "E91.visualSharp", {"position": v(33.78, -11.12) * mm});
            skArc(sketch, "E91.filletArc", {"start": v(34.46, -11.3) * mm, "mid": v(33.91, -11.37) * mm, "end": v(33.55, -11.8) * mm});
            skPoint(sketch, "E92.visualSharp", {"position": v(36.52, -17.83) * mm});
            skArc(sketch, "E92.filletArc", {"start": v(36.35, -18.18) * mm, "mid": v(36.43, -17.82) * mm, "end": v(36.32, -17.47) * mm});
            skPoint(sketch, "E93.visualSharp", {"position": v(32.54, -14.33) * mm});
            skArc(sketch, "E93.filletArc", {"start": v(32.82, -13.69) * mm, "mid": v(32.8, -14.24) * mm, "end": v(33.18, -14.66) * mm});
            skPoint(sketch, "E94.visualSharp", {"position": v(30.72, -17.9) * mm});
            skArc(sketch, "E94.filletArc", {"start": v(31.36, -18.23) * mm, "mid": v(30.8, -18.17) * mm, "end": v(30.36, -18.5) * mm});
            skPoint(sketch, "E95.visualSharp", {"position": v(35.89, -19.07) * mm});
            skArc(sketch, "E95.filletArc", {"start": v(35.48, -19.12) * mm, "mid": v(35.83, -19) * mm, "end": v(36.07, -18.72) * mm});
            skPoint(sketch, "E96.visualSharp", {"position": v(28.85, -20.79) * mm});
            skArc(sketch, "E96.filletArc", {"start": v(29.26, -20.21) * mm, "mid": v(29.13, -20.75) * mm, "end": v(29.4, -21.24) * mm});
            skPoint(sketch, "E97.visualSharp", {"position": v(26.33, -23.9) * mm});
            skArc(sketch, "E97.filletArc", {"start": v(26.89, -24.35) * mm, "mid": v(26.36, -24.18) * mm, "end": v(25.85, -24.42) * mm});
            skPoint(sketch, "E98.visualSharp", {"position": v(31.14, -26.11) * mm});
            skArc(sketch, "E98.filletArc", {"start": v(30.73, -26.08) * mm, "mid": v(31.1, -26.03) * mm, "end": v(31.4, -25.81) * mm});
            skPoint(sketch, "E99.visualSharp", {"position": v(32.02, -25.03) * mm});
            skArc(sketch, "E99.filletArc", {"start": v(31.77, -25.34) * mm, "mid": v(31.92, -25) * mm, "end": v(31.9, -24.64) * mm});
            skPoint(sketch, "E100.visualSharp", {"position": v(26.11, -31.14) * mm});
            skArc(sketch, "E100.filletArc", {"start": v(25.81, -31.4) * mm, "mid": v(26.03, -31.1) * mm, "end": v(26.08, -30.73) * mm});
            skPoint(sketch, "E101.visualSharp", {"position": v(23.9, -26.33) * mm});
            skArc(sketch, "E101.filletArc", {"start": v(24.42, -25.85) * mm, "mid": v(24.18, -26.36) * mm, "end": v(24.35, -26.89) * mm});
            skPoint(sketch, "E102.visualSharp", {"position": v(25.03, -32.02) * mm});
            skArc(sketch, "E102.filletArc", {"start": v(24.64, -31.9) * mm, "mid": v(25, -31.92) * mm, "end": v(25.34, -31.77) * mm});
            skPoint(sketch, "E103.visualSharp", {"position": v(20.79, -28.85) * mm});
            skArc(sketch, "E103.filletArc", {"start": v(21.24, -29.4) * mm, "mid": v(20.75, -29.13) * mm, "end": v(20.21, -29.26) * mm});
            skPoint(sketch, "E104.visualSharp", {"position": v(17.9, -30.72) * mm});
            skArc(sketch, "E104.filletArc", {"start": v(18.5, -30.36) * mm, "mid": v(18.17, -30.8) * mm, "end": v(18.23, -31.36) * mm});
            skPoint(sketch, "E105.visualSharp", {"position": v(19.07, -35.89) * mm});
            skArc(sketch, "E105.filletArc", {"start": v(18.72, -36.07) * mm, "mid": v(19, -35.83) * mm, "end": v(19.12, -35.48) * mm});
            skPoint(sketch, "E106.visualSharp", {"position": v(17.83, -36.52) * mm});
            skArc(sketch, "E106.filletArc", {"start": v(17.47, -36.32) * mm, "mid": v(17.82, -36.43) * mm, "end": v(18.18, -36.35) * mm});
            skPoint(sketch, "E107.visualSharp", {"position": v(14.33, -32.54) * mm});
            skArc(sketch, "E107.filletArc", {"start": v(14.66, -33.18) * mm, "mid": v(14.24, -32.8) * mm, "end": v(13.69, -32.82) * mm});
            skPoint(sketch, "E108.visualSharp", {"position": v(11.12, -33.78) * mm});
            skArc(sketch, "E108.filletArc", {"start": v(11.8, -33.55) * mm, "mid": v(11.37, -33.91) * mm, "end": v(11.3, -34.46) * mm});
            skPoint(sketch, "E109.visualSharp", {"position": v(11.2, -39.07) * mm});
            skArc(sketch, "E109.filletArc", {"start": v(10.81, -39.18) * mm, "mid": v(11.13, -39) * mm, "end": v(11.33, -38.68) * mm});
            skPoint(sketch, "E110.visualSharp", {"position": v(9.84, -39.43) * mm});
            skArc(sketch, "E110.filletArc", {"start": v(9.53, -39.16) * mm, "mid": v(9.86, -39.33) * mm, "end": v(10.23, -39.33) * mm});
            skPoint(sketch, "E111.visualSharp", {"position": v(7.25, -34.81) * mm});
            skArc(sketch, "E111.filletArc", {"start": v(7.44, -35.5) * mm, "mid": v(7.1, -35.05) * mm, "end": v(6.56, -34.95) * mm});
            skPoint(sketch, "E112.visualSharp", {"position": v(3.86, -35.35) * mm});
            skArc(sketch, "E112.filletArc", {"start": v(4.56, -35.27) * mm, "mid": v(4.07, -35.53) * mm, "end": v(3.9, -36.06) * mm});
            skPoint(sketch, "E113.visualSharp", {"position": v(2.82, -40.54) * mm});
            skArc(sketch, "E113.filletArc", {"start": v(2.43, -40.57) * mm, "mid": v(2.78, -40.46) * mm, "end": v(3.04, -40.2) * mm});
            skPoint(sketch, "E114.visualSharp", {"position": v(1.43, -40.61) * mm});
            skArc(sketch, "E114.filletArc", {"start": v(1.18, -40.29) * mm, "mid": v(1.46, -40.52) * mm, "end": v(1.82, -40.6) * mm});
            skPoint(sketch, "E115.visualSharp", {"position": v(-0.14, -35.56) * mm});
            skArc(sketch, "E115.filletArc", {"start": v(-0.1, -36.27) * mm, "mid": v(-0.33, -35.77) * mm, "end": v(-0.85, -35.55) * mm});
            skPoint(sketch, "E116.visualSharp", {"position": v(-3.58, -35.38) * mm});
            skArc(sketch, "E116.filletArc", {"start": v(-2.87, -35.44) * mm, "mid": v(-3.4, -35.6) * mm, "end": v(-3.69, -36.08) * mm});
            skPoint(sketch, "E117.visualSharp", {"position": v(-5.67, -40.24) * mm});
            skArc(sketch, "E117.filletArc", {"start": v(-6.06, -40.19) * mm, "mid": v(-5.7, -40.15) * mm, "end": v(-5.39, -39.94) * mm});
            skPoint(sketch, "E118.visualSharp", {"position": v(-7.05, -40.02) * mm});
            skArc(sketch, "E118.filletArc", {"start": v(-7.22, -39.65) * mm, "mid": v(-7, -39.94) * mm, "end": v(-6.66, -40.1) * mm});
            skPoint(sketch, "E119.visualSharp", {"position": v(-7.53, -34.75) * mm});
            skArc(sketch, "E119.filletArc", {"start": v(-7.64, -35.46) * mm, "mid": v(-7.76, -34.91) * mm, "end": v(-8.22, -34.6) * mm});
            skPoint(sketch, "E120.visualSharp", {"position": v(-10.85, -33.86) * mm});
            skArc(sketch, "E120.filletArc", {"start": v(-10.18, -34.07) * mm, "mid": v(-10.73, -34.12) * mm, "end": v(-11.1, -34.53) * mm});
            skPoint(sketch, "E121.visualSharp", {"position": v(-13.91, -38.19) * mm});
            skArc(sketch, "E121.filletArc", {"start": v(-14.28, -38.05) * mm, "mid": v(-13.91, -38.09) * mm, "end": v(-13.57, -37.95) * mm});
            skPoint(sketch, "E122.visualSharp", {"position": v(-15.21, -37.69) * mm});
            skArc(sketch, "E122.filletArc", {"start": v(-15.3, -37.29) * mm, "mid": v(-15.15, -37.62) * mm, "end": v(-14.85, -37.83) * mm});
            skPoint(sketch, "E123.visualSharp", {"position": v(-14.6, -32.43) * mm});
            skArc(sketch, "E123.filletArc", {"start": v(-14.85, -33.1) * mm, "mid": v(-14.85, -32.54) * mm, "end": v(-15.23, -32.13) * mm});
            skPoint(sketch, "E124.visualSharp", {"position": v(-17.66, -30.87) * mm});
            skArc(sketch, "E124.filletArc", {"start": v(-17.04, -31.21) * mm, "mid": v(-17.6, -31.14) * mm, "end": v(-18.05, -31.46) * mm});
            skPoint(sketch, "E125.visualSharp", {"position": v(-21.55, -34.46) * mm});
            skArc(sketch, "E125.filletArc", {"start": v(-21.88, -34.25) * mm, "mid": v(-21.53, -34.36) * mm, "end": v(-21.17, -34.3) * mm});
            skPoint(sketch, "E126.visualSharp", {"position": v(-22.72, -33.7) * mm});
            skArc(sketch, "E126.filletArc", {"start": v(-22.73, -33.29) * mm, "mid": v(-22.64, -33.65) * mm, "end": v(-22.39, -33.92) * mm});
            skPoint(sketch, "E127.visualSharp", {"position": v(-21.02, -28.69) * mm});
            skArc(sketch, "E127.filletArc", {"start": v(-21.4, -29.28) * mm, "mid": v(-21.3, -28.74) * mm, "end": v(-21.58, -28.26) * mm});
            skPoint(sketch, "E128.visualSharp", {"position": v(-23.69, -26.52) * mm});
            skArc(sketch, "E128.filletArc", {"start": v(-23.16, -26.99) * mm, "mid": v(-23.68, -26.8) * mm, "end": v(-24.2, -27.03) * mm});
            skPoint(sketch, "E129.visualSharp", {"position": v(-28.24, -29.23) * mm});
            skArc(sketch, "E129.filletArc", {"start": v(-28.52, -28.95) * mm, "mid": v(-28.2, -29.14) * mm, "end": v(-27.84, -29.15) * mm});
            skPoint(sketch, "E130.visualSharp", {"position": v(-29.23, -28.24) * mm});
            skArc(sketch, "E130.filletArc", {"start": v(-29.15, -27.84) * mm, "mid": v(-29.14, -28.2) * mm, "end": v(-28.95, -28.52) * mm});
            skPoint(sketch, "E131.visualSharp", {"position": v(-26.52, -23.69) * mm});
            skArc(sketch, "E131.filletArc", {"start": v(-27.03, -24.2) * mm, "mid": v(-26.8, -23.68) * mm, "end": v(-26.99, -23.16) * mm});
            skPoint(sketch, "E132.visualSharp", {"position": v(-28.69, -21.02) * mm});
            skArc(sketch, "E132.filletArc", {"start": v(-28.26, -21.58) * mm, "mid": v(-28.74, -21.3) * mm, "end": v(-29.28, -21.4) * mm});
            skPoint(sketch, "E133.visualSharp", {"position": v(-33.7, -22.72) * mm});
            skArc(sketch, "E133.filletArc", {"start": v(-33.92, -22.39) * mm, "mid": v(-33.65, -22.64) * mm, "end": v(-33.29, -22.73) * mm});
            skPoint(sketch, "E134.visualSharp", {"position": v(-34.46, -21.55) * mm});
            skArc(sketch, "E134.filletArc", {"start": v(-34.3, -21.17) * mm, "mid": v(-34.36, -21.53) * mm, "end": v(-34.25, -21.88) * mm});
            skPoint(sketch, "E135.visualSharp", {"position": v(-30.87, -17.66) * mm});
            skArc(sketch, "E135.filletArc", {"start": v(-31.46, -18.05) * mm, "mid": v(-31.14, -17.6) * mm, "end": v(-31.21, -17.04) * mm});
            skPoint(sketch, "E136.visualSharp", {"position": v(-32.43, -14.6) * mm});
            skArc(sketch, "E136.filletArc", {"start": v(-32.13, -15.23) * mm, "mid": v(-32.54, -14.85) * mm, "end": v(-33.1, -14.85) * mm});
            skPoint(sketch, "E137.visualSharp", {"position": v(-37.69, -15.21) * mm});
            skArc(sketch, "E137.filletArc", {"start": v(-37.83, -14.85) * mm, "mid": v(-37.62, -15.15) * mm, "end": v(-37.29, -15.3) * mm});
            skPoint(sketch, "E138.visualSharp", {"position": v(-38.19, -13.91) * mm});
            skArc(sketch, "E138.filletArc", {"start": v(-37.95, -13.57) * mm, "mid": v(-38.09, -13.91) * mm, "end": v(-38.05, -14.28) * mm});
            skPoint(sketch, "E139.visualSharp", {"position": v(-33.86, -10.85) * mm});
            skArc(sketch, "E139.filletArc", {"start": v(-34.53, -11.1) * mm, "mid": v(-34.12, -10.73) * mm, "end": v(-34.07, -10.18) * mm});
            skPoint(sketch, "E140.visualSharp", {"position": v(-34.75, -7.53) * mm});
            skArc(sketch, "E140.filletArc", {"start": v(-34.6, -8.22) * mm, "mid": v(-34.91, -7.76) * mm, "end": v(-35.46, -7.64) * mm});
            skPoint(sketch, "E141.visualSharp", {"position": v(-40.02, -7.05) * mm});
            skArc(sketch, "E141.filletArc", {"start": v(-40.1, -6.66) * mm, "mid": v(-39.94, -7) * mm, "end": v(-39.65, -7.22) * mm});
            skPoint(sketch, "E142.visualSharp", {"position": v(-40.24, -5.67) * mm});
            skArc(sketch, "E142.filletArc", {"start": v(-39.94, -5.39) * mm, "mid": v(-40.15, -5.7) * mm, "end": v(-40.19, -6.06) * mm});
            skPoint(sketch, "E143.visualSharp", {"position": v(-35.38, -3.58) * mm});
            skArc(sketch, "E143.filletArc", {"start": v(-36.08, -3.69) * mm, "mid": v(-35.6, -3.4) * mm, "end": v(-35.44, -2.87) * mm});
            skPoint(sketch, "E144.visualSharp", {"position": v(-35.56, -0.14) * mm});
            skArc(sketch, "E144.filletArc", {"start": v(-35.55, -0.85) * mm, "mid": v(-35.77, -0.33) * mm, "end": v(-36.27, -0.1) * mm});
            skPoint(sketch, "E145.visualSharp", {"position": v(-40.61, 1.43) * mm});
            skArc(sketch, "E145.filletArc", {"start": v(-40.6, 1.82) * mm, "mid": v(-40.52, 1.46) * mm, "end": v(-40.29, 1.18) * mm});
            skPoint(sketch, "E146.visualSharp", {"position": v(-40.54, 2.82) * mm});
            skArc(sketch, "E146.filletArc", {"start": v(-40.2, 3.04) * mm, "mid": v(-40.46, 2.78) * mm, "end": v(-40.57, 2.43) * mm});
            skPoint(sketch, "E147.visualSharp", {"position": v(-35.35, 3.86) * mm});
            skArc(sketch, "E147.filletArc", {"start": v(-36.06, 3.9) * mm, "mid": v(-35.53, 4.07) * mm, "end": v(-35.27, 4.56) * mm});
            skPoint(sketch, "E148.visualSharp", {"position": v(-34.81, 7.25) * mm});
            skArc(sketch, "E148.filletArc", {"start": v(-34.95, 6.56) * mm, "mid": v(-35.05, 7.1) * mm, "end": v(-35.5, 7.44) * mm});
            skPoint(sketch, "E149.visualSharp", {"position": v(-39.43, 9.84) * mm});
            skArc(sketch, "E149.filletArc", {"start": v(-39.33, 10.23) * mm, "mid": v(-39.33, 9.86) * mm, "end": v(-39.16, 9.53) * mm});
            skPoint(sketch, "E150.visualSharp", {"position": v(-39.07, 11.2) * mm});
            skArc(sketch, "E150.filletArc", {"start": v(-38.68, 11.33) * mm, "mid": v(-39, 11.13) * mm, "end": v(-39.18, 10.81) * mm});
            skPoint(sketch, "E151.visualSharp", {"position": v(-33.78, 11.12) * mm});
            skArc(sketch, "E151.filletArc", {"start": v(-34.46, 11.3) * mm, "mid": v(-33.91, 11.37) * mm, "end": v(-33.55, 11.8) * mm});
            skPoint(sketch, "E152.visualSharp", {"position": v(-32.54, 14.33) * mm});
            skArc(sketch, "E152.filletArc", {"start": v(-32.82, 13.69) * mm, "mid": v(-32.8, 14.24) * mm, "end": v(-33.18, 14.66) * mm});
            skPoint(sketch, "E153.visualSharp", {"position": v(-36.52, 17.83) * mm});
            skArc(sketch, "E153.filletArc", {"start": v(-36.35, 18.18) * mm, "mid": v(-36.43, 17.82) * mm, "end": v(-36.32, 17.47) * mm});
            skPoint(sketch, "E154.visualSharp", {"position": v(-35.89, 19.07) * mm});
            skArc(sketch, "E154.filletArc", {"start": v(-35.48, 19.12) * mm, "mid": v(-35.83, 19) * mm, "end": v(-36.07, 18.72) * mm});
            skPoint(sketch, "E155.visualSharp", {"position": v(-30.72, 17.9) * mm});
            skArc(sketch, "E155.filletArc", {"start": v(-31.36, 18.23) * mm, "mid": v(-30.8, 18.17) * mm, "end": v(-30.36, 18.5) * mm});
            skPoint(sketch, "E156.visualSharp", {"position": v(-28.85, 20.79) * mm});
            skArc(sketch, "E156.filletArc", {"start": v(-29.26, 20.21) * mm, "mid": v(-29.13, 20.75) * mm, "end": v(-29.4, 21.24) * mm});
            skPoint(sketch, "E157.visualSharp", {"position": v(-32.02, 25.03) * mm});
            skArc(sketch, "E157.filletArc", {"start": v(-31.77, 25.34) * mm, "mid": v(-31.92, 25) * mm, "end": v(-31.9, 24.64) * mm});
            skPoint(sketch, "E158.visualSharp", {"position": v(-31.14, 26.11) * mm});
            skArc(sketch, "E158.filletArc", {"start": v(-30.73, 26.08) * mm, "mid": v(-31.1, 26.03) * mm, "end": v(-31.4, 25.81) * mm});
            skPoint(sketch, "E159.visualSharp", {"position": v(-26.33, 23.9) * mm});
            skArc(sketch, "E159.filletArc", {"start": v(-26.89, 24.35) * mm, "mid": v(-26.36, 24.18) * mm, "end": v(-25.85, 24.42) * mm});
            skSolve(sketch);
        }
        {
            var Q0;
            Q0=qSketchRegion(id+"F0",true);
            extrude(context, id + "F1", {"entities" : qUnion([Q0]), "depth" : 114.3 * mm});
        }
        {
            var Q0;
            Q0=makeQuery(id+"F1.opExtrude","CAP_FACE",FACE,{"disambiguationData":[OSD([sQuery(id+"F0.wireOp",EDGE,"E0"),sQuery(id+"F0.wireOp",EDGE,"E1"),sQuery(id+"F0.wireOp",EDGE,"E2.trimOffspring"),sQuery(id+"F0.wireOp",EDGE,"E3"),sQuery(id+"F0.wireOp",EDGE,"E4"),sQuery(id+"F0.wireOp",EDGE,"E5.MirrorCS"),sQuery(id+"F0.wireOp",EDGE,"E6.MirrorCS"),sQuery(id+"F0.wireOp",EDGE,"E7.MirrorCS"),sQuery(id+"F0.wireOp",EDGE,"E8.1.0"),sQuery(id+"F0.wireOp",EDGE,"E8.1.1"),sQuery(id+"F0.wireOp",EDGE,"E8.1.2"),sQuery(id+"F0.wireOp",EDGE,"E8.1.3"),sQuery(id+"F0.wireOp",EDGE,"E8.1.4"),sQuery(id+"F0.wireOp",EDGE,"E8.1.5"),sQuery(id+"F0.wireOp",EDGE,"E8.2.0"),sQuery(id+"F0.wireOp",EDGE,"E8.2.1"),sQuery(id+"F0.wireOp",EDGE,"E8.2.2"),sQuery(id+"F0.wireOp",EDGE,"E8.2.3"),sQuery(id+"F0.wireOp",EDGE,"E8.2.4"),sQuery(id+"F0.wireOp",EDGE,"E8.2.5"),sQuery(id+"F0.wireOp",EDGE,"E9.2.3.0"),sQuery(id+"F0.wireOp",EDGE,"E9.4.3.0"),sQuery(id+"F0.wireOp",EDGE,"E9.7.3.0"),sQuery(id+"F0.wireOp",EDGE,"E9.10.3.0"),sQuery(id+"F0.wireOp",EDGE,"E9.14.3.0"),sQuery(id+"F0.wireOp",EDGE,"E9.17.3.0"),sQuery(id+"F0.wireOp",EDGE,"E9.2.4.0"),sQuery(id+"F0.wireOp",EDGE,"E9.4.4.0"),sQuery(id+"F0.wireOp",EDGE,"E9.7.4.0"),sQuery(id+"F0.wireOp",EDGE,"E9.10.4.0"),sQuery(id+"F0.wireOp",EDGE,"E9.14.4.0"),sQuery(id+"F0.wireOp",EDGE,"E9.17.4.0"),sQuery(id+"F0.wireOp",EDGE,"E9.2.5.0"),sQuery(id+"F0.wireOp",EDGE,"E9.4.5.0"),sQuery(id+"F0.wireOp",EDGE,"E9.7.5.0"),sQuery(id+"F0.wireOp",EDGE,"E9.10.5.0"),sQuery(id+"F0.wireOp",EDGE,"E9.14.5.0"),sQuery(id+"F0.wireOp",EDGE,"E9.17.5.0"),sQuery(id+"F0.wireOp",EDGE,"E9.2.6.0"),sQuery(id+"F0.wireOp",EDGE,"E9.4.6.0"),sQuery(id+"F0.wireOp",EDGE,"E9.7.6.0"),sQuery(id+"F0.wireOp",EDGE,"E9.10.6.0"),sQuery(id+"F0.wireOp",EDGE,"E9.14.6.0"),sQuery(id+"F0.wireOp",EDGE,"E9.17.6.0"),sQuery(id+"F0.wireOp",EDGE,"E9.2.7.0"),sQuery(id+"F0.wireOp",EDGE,"E9.4.7.0"),sQuery(id+"F0.wireOp",EDGE,"E9.7.7.0"),sQuery(id+"F0.wireOp",EDGE,"E9.10.7.0"),sQuery(id+"F0.wireOp",EDGE,"E9.14.7.0"),sQuery(id+"F0.wireOp",EDGE,"E9.17.7.0"),sQuery(id+"F0.wireOp",EDGE,"E9.2.8.0"),sQuery(id+"F0.wireOp",EDGE,"E9.4.8.0"),sQuery(id+"F0.wireOp",EDGE,"E9.7.8.0"),sQuery(id+"F0.wireOp",EDGE,"E9.10.8.0"),sQuery(id+"F0.wireOp",EDGE,"E9.14.8.0"),sQuery(id+"F0.wireOp",EDGE,"E9.17.8.0"),sQuery(id+"F0.wireOp",EDGE,"E9.2.9.0"),sQuery(id+"F0.wireOp",EDGE,"E9.4.9.0"),sQuery(id+"F0.wireOp",EDGE,"E9.7.9.0"),sQuery(id+"F0.wireOp",EDGE,"E9.10.9.0"),sQuery(id+"F0.wireOp",EDGE,"E9.14.9.0"),sQuery(id+"F0.wireOp",EDGE,"E9.17.9.0"),sQuery(id+"F0.wireOp",EDGE,"E9.2.10.0"),sQuery(id+"F0.wireOp",EDGE,"E9.4.10.0"),sQuery(id+"F0.wireOp",EDGE,"E9.7.10.0"),sQuery(id+"F0.wireOp",EDGE,"E9.10.10.0"),sQuery(id+"F0.wireOp",EDGE,"E9.14.10.0"),sQuery(id+"F0.wireOp",EDGE,"E9.17.10.0"),sQuery(id+"F0.wireOp",EDGE,"E9.2.11.0"),sQuery(id+"F0.wireOp",EDGE,"E9.4.11.0"),sQuery(id+"F0.wireOp",EDGE,"E9.7.11.0"),sQuery(id+"F0.wireOp",EDGE,"E9.10.11.0"),sQuery(id+"F0.wireOp",EDGE,"E9.14.11.0"),sQuery(id+"F0.wireOp",EDGE,"E9.17.11.0"),sQuery(id+"F0.wireOp",EDGE,"E9.2.12.0"),sQuery(id+"F0.wireOp",EDGE,"E9.4.12.0"),sQuery(id+"F0.wireOp",EDGE,"E9.7.12.0"),sQuery(id+"F0.wireOp",EDGE,"E9.10.12.0"),sQuery(id+"F0.wireOp",EDGE,"E9.14.12.0"),sQuery(id+"F0.wireOp",EDGE,"E9.17.12.0"),sQuery(id+"F0.wireOp",EDGE,"E9.2.13.0"),sQuery(id+"F0.wireOp",EDGE,"E9.4.13.0"),sQuery(id+"F0.wireOp",EDGE,"E9.7.13.0"),sQuery(id+"F0.wireOp",EDGE,"E9.10.13.0"),sQuery(id+"F0.wireOp",EDGE,"E9.14.13.0"),sQuery(id+"F0.wireOp",EDGE,"E9.17.13.0"),sQuery(id+"F0.wireOp",EDGE,"E9.2.14.0"),sQuery(id+"F0.wireOp",EDGE,"E9.4.14.0"),sQuery(id+"F0.wireOp",EDGE,"E9.7.14.0"),sQuery(id+"F0.wireOp",EDGE,"E9.10.14.0"),sQuery(id+"F0.wireOp",EDGE,"E9.14.14.0"),sQuery(id+"F0.wireOp",EDGE,"E9.17.14.0"),sQuery(id+"F0.wireOp",EDGE,"E9.2.15.0"),sQuery(id+"F0.wireOp",EDGE,"E9.4.15.0"),sQuery(id+"F0.wireOp",EDGE,"E9.7.15.0"),sQuery(id+"F0.wireOp",EDGE,"E9.10.15.0"),sQuery(id+"F0.wireOp",EDGE,"E9.14.15.0"),sQuery(id+"F0.wireOp",EDGE,"E9.17.15.0"),sQuery(id+"F0.wireOp",EDGE,"E9.2.16.0"),sQuery(id+"F0.wireOp",EDGE,"E9.4.16.0"),sQuery(id+"F0.wireOp",EDGE,"E9.7.16.0"),sQuery(id+"F0.wireOp",EDGE,"E9.10.16.0"),sQuery(id+"F0.wireOp",EDGE,"E9.14.16.0"),sQuery(id+"F0.wireOp",EDGE,"E9.17.16.0"),sQuery(id+"F0.wireOp",EDGE,"E9.2.17.0"),sQuery(id+"F0.wireOp",EDGE,"E9.4.17.0"),sQuery(id+"F0.wireOp",EDGE,"E9.7.17.0"),sQuery(id+"F0.wireOp",EDGE,"E9.10.17.0"),sQuery(id+"F0.wireOp",EDGE,"E9.14.17.0"),sQuery(id+"F0.wireOp",EDGE,"E9.17.17.0"),sQuery(id+"F0.wireOp",EDGE,"E9.2.18.0"),sQuery(id+"F0.wireOp",EDGE,"E9.4.18.0"),sQuery(id+"F0.wireOp",EDGE,"E9.7.18.0"),sQuery(id+"F0.wireOp",EDGE,"E9.10.18.0"),sQuery(id+"F0.wireOp",EDGE,"E9.14.18.0"),sQuery(id+"F0.wireOp",EDGE,"E9.17.18.0"),sQuery(id+"F0.wireOp",EDGE,"E9.2.19.0"),sQuery(id+"F0.wireOp",EDGE,"E9.4.19.0"),sQuery(id+"F0.wireOp",EDGE,"E9.7.19.0"),sQuery(id+"F0.wireOp",EDGE,"E9.10.19.0"),sQuery(id+"F0.wireOp",EDGE,"E9.14.19.0"),sQuery(id+"F0.wireOp",EDGE,"E9.17.19.0"),sQuery(id+"F0.wireOp",EDGE,"E9.2.20.0"),sQuery(id+"F0.wireOp",EDGE,"E9.4.20.0"),sQuery(id+"F0.wireOp",EDGE,"E9.7.20.0"),sQuery(id+"F0.wireOp",EDGE,"E9.10.20.0"),sQuery(id+"F0.wireOp",EDGE,"E9.14.20.0"),sQuery(id+"F0.wireOp",EDGE,"E9.17.20.0"),sQuery(id+"F0.wireOp",EDGE,"E9.2.21.0"),sQuery(id+"F0.wireOp",EDGE,"E9.4.21.0"),sQuery(id+"F0.wireOp",EDGE,"E9.7.21.0"),sQuery(id+"F0.wireOp",EDGE,"E9.10.21.0"),sQuery(id+"F0.wireOp",EDGE,"E9.14.21.0"),sQuery(id+"F0.wireOp",EDGE,"E9.17.21.0"),sQuery(id+"F0.wireOp",EDGE,"E9.2.22.0"),sQuery(id+"F0.wireOp",EDGE,"E9.4.22.0"),sQuery(id+"F0.wireOp",EDGE,"E9.7.22.0"),sQuery(id+"F0.wireOp",EDGE,"E9.10.22.0"),sQuery(id+"F0.wireOp",EDGE,"E9.14.22.0"),sQuery(id+"F0.wireOp",EDGE,"E9.17.22.0"),sQuery(id+"F0.wireOp",EDGE,"E9.2.23.0"),sQuery(id+"F0.wireOp",EDGE,"E9.4.23.0"),sQuery(id+"F0.wireOp",EDGE,"E9.7.23.0"),sQuery(id+"F0.wireOp",EDGE,"E9.10.23.0"),sQuery(id+"F0.wireOp",EDGE,"E9.14.23.0"),sQuery(id+"F0.wireOp",EDGE,"E9.17.23.0"),sQuery(id+"F0.wireOp",EDGE,"E9.2.24.0"),sQuery(id+"F0.wireOp",EDGE,"E9.4.24.0"),sQuery(id+"F0.wireOp",EDGE,"E9.7.24.0"),sQuery(id+"F0.wireOp",EDGE,"E9.10.24.0"),sQuery(id+"F0.wireOp",EDGE,"E9.14.24.0"),sQuery(id+"F0.wireOp",EDGE,"E9.17.24.0"),sQuery(id+"F0.wireOp",EDGE,"E9.2.25.0"),sQuery(id+"F0.wireOp",EDGE,"E9.4.25.0"),sQuery(id+"F0.wireOp",EDGE,"E9.7.25.0"),sQuery(id+"F0.wireOp",EDGE,"E9.10.25.0"),sQuery(id+"F0.wireOp",EDGE,"E9.14.25.0"),sQuery(id+"F0.wireOp",EDGE,"E9.17.25.0"),sQuery(id+"F0.wireOp",EDGE,"E9.2.26.0"),sQuery(id+"F0.wireOp",EDGE,"E9.4.26.0"),sQuery(id+"F0.wireOp",EDGE,"E9.7.26.0"),sQuery(id+"F0.wireOp",EDGE,"E9.10.26.0"),sQuery(id+"F0.wireOp",EDGE,"E9.14.26.0"),sQuery(id+"F0.wireOp",EDGE,"E9.17.26.0"),sQuery(id+"F0.wireOp",EDGE,"E9.2.27.0"),sQuery(id+"F0.wireOp",EDGE,"E9.4.27.0"),sQuery(id+"F0.wireOp",EDGE,"E9.7.27.0"),sQuery(id+"F0.wireOp",EDGE,"E9.10.27.0"),sQuery(id+"F0.wireOp",EDGE,"E9.14.27.0"),sQuery(id+"F0.wireOp",EDGE,"E9.17.27.0"),sQuery(id+"F0.wireOp",EDGE,"E9.2.28.0"),sQuery(id+"F0.wireOp",EDGE,"E9.4.28.0"),sQuery(id+"F0.wireOp",EDGE,"E9.7.28.0"),sQuery(id+"F0.wireOp",EDGE,"E9.10.28.0"),sQuery(id+"F0.wireOp",EDGE,"E9.14.28.0"),sQuery(id+"F0.wireOp",EDGE,"E9.17.28.0"),sQuery(id+"F0.wireOp",EDGE,"E9.2.29.0"),sQuery(id+"F0.wireOp",EDGE,"E9.4.29.0"),sQuery(id+"F0.wireOp",EDGE,"E9.7.29.0"),sQuery(id+"F0.wireOp",EDGE,"E9.10.29.0"),sQuery(id+"F0.wireOp",EDGE,"E9.14.29.0"),sQuery(id+"F0.wireOp",EDGE,"E9.17.29.0"),sQuery(id+"F0.wireOp",EDGE,"E10.trimOffspring"),sQuery(id+"F0.wireOp",EDGE,"E11.trimOffspring"),sQuery(id+"F0.wireOp",EDGE,"E12.trimOffspring"),sQuery(id+"F0.wireOp",EDGE,"E13.trimOffspring"),sQuery(id+"F0.wireOp",EDGE,"E14.trimOffspring"),sQuery(id+"F0.wireOp",EDGE,"E15.trimOffspring"),sQuery(id+"F0.wireOp",EDGE,"E16.trimOffspring"),sQuery(id+"F0.wireOp",EDGE,"E17.trimOffspring"),sQuery(id+"F0.wireOp",EDGE,"E18.trimOffspring"),sQuery(id+"F0.wireOp",EDGE,"E19.trimOffspring"),sQuery(id+"F0.wireOp",EDGE,"E20.trimOffspring"),sQuery(id+"F0.wireOp",EDGE,"E21.trimOffspring"),sQuery(id+"F0.wireOp",EDGE,"E22.trimOffspring"),sQuery(id+"F0.wireOp",EDGE,"E23.trimOffspring"),sQuery(id+"F0.wireOp",EDGE,"E24.trimOffspring"),sQuery(id+"F0.wireOp",EDGE,"E25.trimOffspring"),sQuery(id+"F0.wireOp",EDGE,"E26.trimOffspring"),sQuery(id+"F0.wireOp",EDGE,"E27.trimOffspring"),sQuery(id+"F0.wireOp",EDGE,"E28.trimOffspring"),sQuery(id+"F0.wireOp",EDGE,"E29.trimOffspring"),sQuery(id+"F0.wireOp",EDGE,"E30.trimOffspring"),sQuery(id+"F0.wireOp",EDGE,"E31.trimOffspring"),sQuery(id+"F0.wireOp",EDGE,"E32.trimOffspring"),sQuery(id+"F0.wireOp",EDGE,"E33.trimOffspring"),sQuery(id+"F0.wireOp",EDGE,"E34.trimOffspring"),sQuery(id+"F0.wireOp",EDGE,"E35.trimOffspring"),sQuery(id+"F0.wireOp",EDGE,"E36.trimOffspring"),sQuery(id+"F0.wireOp",EDGE,"E37.trimOffspring"),sQuery(id+"F0.wireOp",EDGE,"E38.trimOffspring"),sQuery(id+"F0.wireOp",EDGE,"E39.filletArc"),sQuery(id+"F0.wireOp",EDGE,"E40.filletArc"),sQuery(id+"F0.wireOp",EDGE,"E41.filletArc"),sQuery(id+"F0.wireOp",EDGE,"E42.filletArc"),sQuery(id+"F0.wireOp",EDGE,"E43.filletArc"),sQuery(id+"F0.wireOp",EDGE,"E44.filletArc"),sQuery(id+"F0.wireOp",EDGE,"E45.filletArc"),sQuery(id+"F0.wireOp",EDGE,"E46.filletArc"),sQuery(id+"F0.wireOp",EDGE,"E47.filletArc"),sQuery(id+"F0.wireOp",EDGE,"E48.filletArc"),sQuery(id+"F0.wireOp",EDGE,"E49.filletArc"),sQuery(id+"F0.wireOp",EDGE,"E50.filletArc"),sQuery(id+"F0.wireOp",EDGE,"E51.filletArc"),sQuery(id+"F0.wireOp",EDGE,"E52.filletArc"),sQuery(id+"F0.wireOp",EDGE,"E53.filletArc"),sQuery(id+"F0.wireOp",EDGE,"E54.filletArc"),sQuery(id+"F0.wireOp",EDGE,"E55.filletArc"),sQuery(id+"F0.wireOp",EDGE,"E56.filletArc"),sQuery(id+"F0.wireOp",EDGE,"E57.filletArc"),sQuery(id+"F0.wireOp",EDGE,"E58.filletArc"),sQuery(id+"F0.wireOp",EDGE,"E59.filletArc"),sQuery(id+"F0.wireOp",EDGE,"E60.filletArc"),sQuery(id+"F0.wireOp",EDGE,"E61.filletArc"),sQuery(id+"F0.wireOp",EDGE,"E62.filletArc"),sQuery(id+"F0.wireOp",EDGE,"E63.filletArc"),sQuery(id+"F0.wireOp",EDGE,"E64.filletArc"),sQuery(id+"F0.wireOp",EDGE,"E65.filletArc"),sQuery(id+"F0.wireOp",EDGE,"E66.filletArc"),sQuery(id+"F0.wireOp",EDGE,"E67.filletArc"),sQuery(id+"F0.wireOp",EDGE,"E68.filletArc"),sQuery(id+"F0.wireOp",EDGE,"E69.filletArc"),sQuery(id+"F0.wireOp",EDGE,"E70.filletArc"),sQuery(id+"F0.wireOp",EDGE,"E71.filletArc"),sQuery(id+"F0.wireOp",EDGE,"E72.filletArc"),sQuery(id+"F0.wireOp",EDGE,"E73.filletArc"),sQuery(id+"F0.wireOp",EDGE,"E74.filletArc"),sQuery(id+"F0.wireOp",EDGE,"E75.filletArc"),sQuery(id+"F0.wireOp",EDGE,"E76.filletArc"),sQuery(id+"F0.wireOp",EDGE,"E77.filletArc"),sQuery(id+"F0.wireOp",EDGE,"E78.filletArc"),sQuery(id+"F0.wireOp",EDGE,"E79.filletArc"),sQuery(id+"F0.wireOp",EDGE,"E80.filletArc"),sQuery(id+"F0.wireOp",EDGE,"E81.filletArc"),sQuery(id+"F0.wireOp",EDGE,"E82.filletArc"),sQuery(id+"F0.wireOp",EDGE,"E83.filletArc"),sQuery(id+"F0.wireOp",EDGE,"E84.filletArc"),sQuery(id+"F0.wireOp",EDGE,"E85.filletArc"),sQuery(id+"F0.wireOp",EDGE,"E86.filletArc"),sQuery(id+"F0.wireOp",EDGE,"E87.filletArc"),sQuery(id+"F0.wireOp",EDGE,"E88.filletArc"),sQuery(id+"F0.wireOp",EDGE,"E89.filletArc"),sQuery(id+"F0.wireOp",EDGE,"E90.filletArc"),sQuery(id+"F0.wireOp",EDGE,"E91.filletArc"),sQuery(id+"F0.wireOp",EDGE,"E92.filletArc"),sQuery(id+"F0.wireOp",EDGE,"E93.filletArc"),sQuery(id+"F0.wireOp",EDGE,"E94.filletArc"),sQuery(id+"F0.wireOp",EDGE,"E95.filletArc"),sQuery(id+"F0.wireOp",EDGE,"E96.filletArc"),sQuery(id+"F0.wireOp",EDGE,"E97.filletArc"),sQuery(id+"F0.wireOp",EDGE,"E98.filletArc"),sQuery(id+"F0.wireOp",EDGE,"E99.filletArc"),sQuery(id+"F0.wireOp",EDGE,"E100.filletArc"),sQuery(id+"F0.wireOp",EDGE,"E101.filletArc"),sQuery(id+"F0.wireOp",EDGE,"E102.filletArc"),sQuery(id+"F0.wireOp",EDGE,"E103.filletArc"),sQuery(id+"F0.wireOp",EDGE,"E104.filletArc"),sQuery(id+"F0.wireOp",EDGE,"E105.filletArc"),sQuery(id+"F0.wireOp",EDGE,"E106.filletArc"),sQuery(id+"F0.wireOp",EDGE,"E107.filletArc"),sQuery(id+"F0.wireOp",EDGE,"E108.filletArc"),sQuery(id+"F0.wireOp",EDGE,"E109.filletArc"),sQuery(id+"F0.wireOp",EDGE,"E110.filletArc"),sQuery(id+"F0.wireOp",EDGE,"E111.filletArc"),sQuery(id+"F0.wireOp",EDGE,"E112.filletArc"),sQuery(id+"F0.wireOp",EDGE,"E113.filletArc"),sQuery(id+"F0.wireOp",EDGE,"E114.filletArc"),sQuery(id+"F0.wireOp",EDGE,"E115.filletArc"),sQuery(id+"F0.wireOp",EDGE,"E116.filletArc"),sQuery(id+"F0.wireOp",EDGE,"E117.filletArc"),sQuery(id+"F0.wireOp",EDGE,"E118.filletArc"),sQuery(id+"F0.wireOp",EDGE,"E119.filletArc"),sQuery(id+"F0.wireOp",EDGE,"E120.filletArc"),sQuery(id+"F0.wireOp",EDGE,"E121.filletArc"),sQuery(id+"F0.wireOp",EDGE,"E122.filletArc"),sQuery(id+"F0.wireOp",EDGE,"E123.filletArc"),sQuery(id+"F0.wireOp",EDGE,"E124.filletArc"),sQuery(id+"F0.wireOp",EDGE,"E125.filletArc"),sQuery(id+"F0.wireOp",EDGE,"E126.filletArc"),sQuery(id+"F0.wireOp",EDGE,"E127.filletArc"),sQuery(id+"F0.wireOp",EDGE,"E128.filletArc"),sQuery(id+"F0.wireOp",EDGE,"E129.filletArc"),sQuery(id+"F0.wireOp",EDGE,"E130.filletArc"),sQuery(id+"F0.wireOp",EDGE,"E131.filletArc"),sQuery(id+"F0.wireOp",EDGE,"E132.filletArc"),sQuery(id+"F0.wireOp",EDGE,"E133.filletArc"),sQuery(id+"F0.wireOp",EDGE,"E134.filletArc"),sQuery(id+"F0.wireOp",EDGE,"E135.filletArc"),sQuery(id+"F0.wireOp",EDGE,"E136.filletArc"),sQuery(id+"F0.wireOp",EDGE,"E137.filletArc"),sQuery(id+"F0.wireOp",EDGE,"E138.filletArc"),sQuery(id+"F0.wireOp",EDGE,"E139.filletArc"),sQuery(id+"F0.wireOp",EDGE,"E140.filletArc"),sQuery(id+"F0.wireOp",EDGE,"E141.filletArc"),sQuery(id+"F0.wireOp",EDGE,"E142.filletArc"),sQuery(id+"F0.wireOp",EDGE,"E143.filletArc"),sQuery(id+"F0.wireOp",EDGE,"E144.filletArc"),sQuery(id+"F0.wireOp",EDGE,"E145.filletArc"),sQuery(id+"F0.wireOp",EDGE,"E146.filletArc"),sQuery(id+"F0.wireOp",EDGE,"E147.filletArc"),sQuery(id+"F0.wireOp",EDGE,"E148.filletArc"),sQuery(id+"F0.wireOp",EDGE,"E149.filletArc"),sQuery(id+"F0.wireOp",EDGE,"E150.filletArc"),sQuery(id+"F0.wireOp",EDGE,"E151.filletArc"),sQuery(id+"F0.wireOp",EDGE,"E152.filletArc"),sQuery(id+"F0.wireOp",EDGE,"E153.filletArc"),sQuery(id+"F0.wireOp",EDGE,"E154.filletArc"),sQuery(id+"F0.wireOp",EDGE,"E155.filletArc"),sQuery(id+"F0.wireOp",EDGE,"E156.filletArc"),sQuery(id+"F0.wireOp",EDGE,"E157.filletArc"),sQuery(id+"F0.wireOp",EDGE,"E158.filletArc"),sQuery(id+"F0.wireOp",EDGE,"E159.filletArc")])],"isStart":false});
            var sketch = newSketch(context, id + "F2", { "sketchPlane" : qUnion([Q0])});
            skCircle(sketch, "E160", {"center": v(0, 0) * mm, "radius": 19.05 * mm});
            skSolve(sketch);
        }
        {
            var Q0;
            Q0=makeQuery(id+"F2.imprint","IMPRINT",FACE,{"disambiguationData":[TD([[makeQuery(id+"F2.imprint","IMPRINT",EDGE,{"derivedFrom":sQuery(id+"F2.wireOp",EDGE,"E160")}),1.0]])]});
            extrude(context, id + "F3", {"entities" : qUnion([Q0]), "operationType" : NewBodyOperationType.ADD, "depth" : 12.7 * mm});
        }
    });
